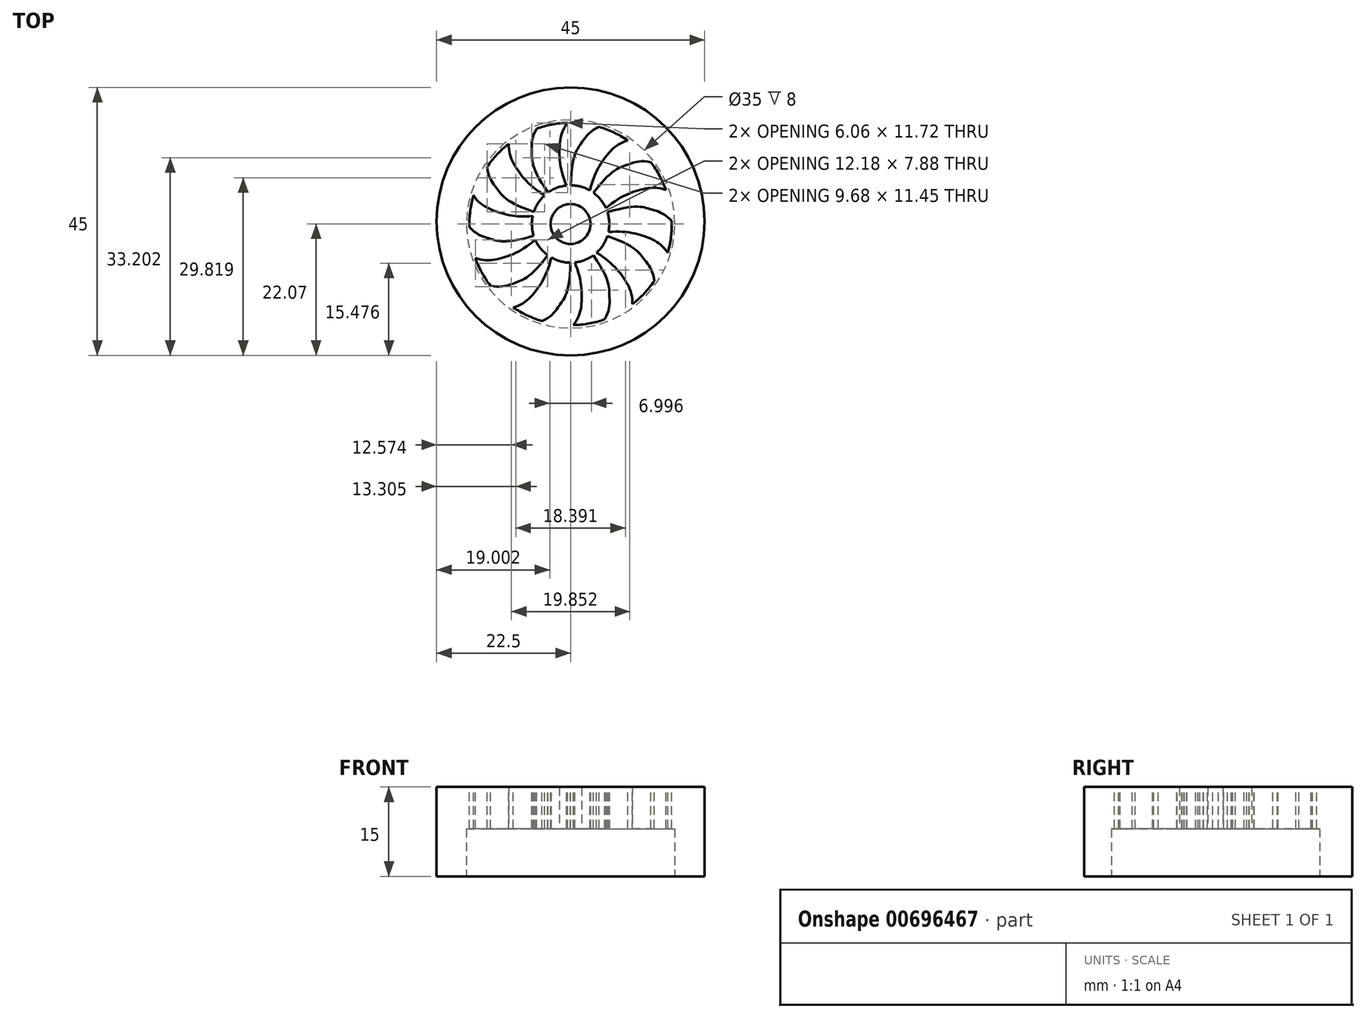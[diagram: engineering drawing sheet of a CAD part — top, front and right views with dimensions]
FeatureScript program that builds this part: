
annotation { "Feature Type Name" : "Feature", "Feature Type Description" : "" }
export const myFeature = defineFeature(function(context is Context, id is Id, definition is map)
    precondition{}
    {
        {
            var Q0;
            Q0=qCreatedBy(makeId("Top.planeOp"),FACE);
            var sketch = newSketch(context, id + "F0", { "sketchPlane" : qUnion([Q0])});
            skCircle(sketch, "E0", {"center": v(0, 0) * mm, "radius": 22.5 * mm});
            skSolve(sketch);
        }
        {
            var Q0;
            Q0=makeQuery(id+"F0.imprint","IMPRINT",FACE,{"disambiguationData":[TD([[makeQuery(id+"F0.imprint","IMPRINT",EDGE,{"derivedFrom":sQuery(id+"F0.wireOp",EDGE,"E0")}),1.0]])]});
            extrude(context, id + "F1", {"entities" : qUnion([Q0]), "depth" : 15 * mm, "offsetDistance" : 25 * mm});
        }
        {
            var Q0;
            Q0=qCreatedBy(makeId("Front.planeOp"),FACE);
            var sketch = newSketch(context, id + "F2", { "sketchPlane" : qUnion([Q0])});
            skLineSegment(sketch, "E1", {"start": v(0, 22.22) * mm, "end": v(0, -15.86) * mm});
            skSolve(sketch);
        }
        {
            var Q0;
            Q0=makeQuery(id+"F1.opExtrude","CAP_FACE",FACE,{"disambiguationData":[OSD([sQuery(id+"F0.wireOp",EDGE,"E0")])],"isStart":false});
            var sketch = newSketch(context, id + "F3", { "sketchPlane" : qUnion([Q0])});
            skFitSpline(sketch, "E2", {"points": [v(0, 5) * mm, v(-1.86, 12.83) * mm, v(0, 17.5) * mm], "startDerivative": vector(-8.9, 17.17) * mm, "endDerivative": vector(9.6, 9.27) * mm});
            skFitSpline(sketch, "E3", {"points": [v(0, 5) * mm, v(1.84, 13.62) * mm, v(5.55, 16.6) * mm], "startDerivative": vector(0, 33.37) * mm, "endDerivative": vector(16.62, 5.33) * mm});
            skArc(sketch, "E4", {"start": v(5.55, 16.6) * mm, "mid": v(2.81, 17.27) * mm, "end": v(0, 17.5) * mm});
            skSolve(sketch);
        }
        {
            var Q0;
            Q0=makeQuery(id+"F3.imprint","IMPRINT",FACE,{"disambiguationData":[TD([[makeQuery(id+"F3.imprint","IMPRINT",EDGE,{"derivedFrom":sQuery(id+"F3.wireOp",EDGE,"E2")}),-1.0]])]});
            var Q1;
            Q1=sQuery(id+"F3.wireOp",EDGE,"E3");
            var Q2;
            Q2=sQuery(id+"F3.wireOp",EDGE,"E2");
            var Q3;
            Q3=sQuery(id+"F3.wireOp",EDGE,"E4");
            extrude(context, id + "F4", {"entities" : qUnion([Q0]), "operationType" : NewBodyOperationType.INTERSECT, "surfaceEntities" : qUnion([Q1, Q2, Q3]), "endBound" : BoundingType.THROUGH_ALL, "oppositeDirection" : true, "depth" : 25 * mm, "offsetDistance" : 25 * mm});
        }
        {
            var Q0;
            Q0=makeQuery(id+"F1.opExtrude","SWEPT_BODY",BODY,{"disambiguationData":[OSD([sQuery(id+"F0.wireOp",EDGE,"E0")])]});
            var Q1;
            Q1=sQuery(id+"F2.wireOp",EDGE,"E1");
            circularPattern(context, id + "F5", {"entities" : qUnion([Q0]), "axis" : qUnion([Q1]), "angle" : 360 * degree, "instanceCount" : 10, "equalSpace" : true});
        }
        {
            var Q0;
            Q0=makeQuery(id+"F3.imprint","IMPRINT",FACE,{"disambiguationData":[TD([[makeQuery(id+"F3.imprint","IMPRINT",EDGE,{"derivedFrom":sQuery(id+"F3.wireOp",EDGE,"E2")}),1.0]])]});
            var sketch = newSketch(context, id + "F6", { "sketchPlane" : qUnion([Q0])});
            skCircle(sketch, "E5", {"center": v(0, 0) * mm, "radius": 17 * mm});
            skCircle(sketch, "E6", {"center": v(0, 0.43) * mm, "radius": 22.5 * mm});
            skSolve(sketch);
        }
        {
            var Q0;
            Q0 = qSketchRegion(id + "F6", true);
            extrude(context, id + "F7", {"entities" : qUnion([Q0]), "operationType" : NewBodyOperationType.ADD, "oppositeDirection" : true, "depth" : 15 * mm, "offsetDistance" : 25 * mm});
        }
        {
            var Q0;
            Q0=makeQuery(id+"F3.imprint","IMPRINT",FACE,{"disambiguationData":[TD([[makeQuery(id+"F3.imprint","IMPRINT",EDGE,{"derivedFrom":sQuery(id+"F3.wireOp",EDGE,"E2")}),-1.0]])]});
            var sketch = newSketch(context, id + "F8", { "sketchPlane" : qUnion([Q0])});
            skCircle(sketch, "E7", {"center": v(0, 0) * mm, "radius": 6.5 * mm});
            skSolve(sketch);
        }
        {
            var Q0;
            Q0 = qSketchRegion(id + "F8", true);
            extrude(context, id + "F9", {"entities" : qUnion([Q0]), "operationType" : NewBodyOperationType.ADD, "oppositeDirection" : true, "depth" : 15 * mm, "offsetDistance" : 25 * mm});
        }
        {
            var Q0;
            {var subQ0=makeQuery(id+"F1.opExtrude","CAP_FACE",FACE,{"disambiguationData":[OSD([sQuery(id+"F0.wireOp",EDGE,"E0")])],"isStart":true});Q0=makeQuery(id+"F9.boolean.opBoolean","MERGE",FACE,{"derivedFrom":[makeQuery(id+"F7.boolean.opBoolean","MERGE",FACE,{"derivedFrom":[subQ0,makeQuery(id+"F5.opPattern","COPY",FACE,{"derivedFrom":subQ0,"instanceName":"1"}),makeQuery(id+"F5.opPattern","COPY",FACE,{"derivedFrom":subQ0,"instanceName":"2"}),makeQuery(id+"F5.opPattern","COPY",FACE,{"derivedFrom":subQ0,"instanceName":"3"}),makeQuery(id+"F5.opPattern","COPY",FACE,{"derivedFrom":subQ0,"instanceName":"4"}),makeQuery(id+"F5.opPattern","COPY",FACE,{"derivedFrom":subQ0,"instanceName":"5"}),makeQuery(id+"F5.opPattern","COPY",FACE,{"derivedFrom":subQ0,"instanceName":"6"}),makeQuery(id+"F5.opPattern","COPY",FACE,{"derivedFrom":subQ0,"instanceName":"7"}),makeQuery(id+"F5.opPattern","COPY",FACE,{"derivedFrom":subQ0,"instanceName":"8"}),makeQuery(id+"F5.opPattern","COPY",FACE,{"derivedFrom":subQ0,"instanceName":"9"}),makeQuery(id+"F7.opExtrude","CAP_FACE",FACE,{"disambiguationData":[OSD([sQuery(id+"F6.wireOp",EDGE,"E5"),sQuery(id+"F6.wireOp",EDGE,"E6")])],"isStart":false})]}),makeQuery(id+"F9.opExtrude","CAP_FACE",FACE,{"disambiguationData":[OSD([sQuery(id+"F8.wireOp",EDGE,"E7")])],"isStart":false})]});}
            var sketch = newSketch(context, id + "F10", { "sketchPlane" : qUnion([Q0])});
            skCircle(sketch, "E8", {"center": v(0, 0) * mm, "radius": 17.5 * mm});
            skSolve(sketch);
        }
        {
            var Q0;
            Q0 = qSketchRegion(id + "F10", true);
            extrude(context, id + "F11", {"entities" : qUnion([Q0]), "operationType" : NewBodyOperationType.REMOVE, "oppositeDirection" : true, "depth" : 8 * mm, "offsetDistance" : 25 * mm});
        }
        {
            var Q0;
            Q0=makeQuery(id+"F3.imprint","IMPRINT",FACE,{"disambiguationData":[TD([[makeQuery(id+"F3.imprint","IMPRINT",EDGE,{"derivedFrom":sQuery(id+"F3.wireOp",EDGE,"E2")}),1.0]])]});
            var sketch = newSketch(context, id + "F12", { "sketchPlane" : qUnion([Q0])});
            skCircle(sketch, "E9", {"center": v(0, 0) * mm, "radius": 3.35 * mm});
            skSolve(sketch);
        }
        {
            var Q0;
            Q0 = qSketchRegion(id + "F12", true);
            extrude(context, id + "F13", {"entities" : qUnion([Q0]), "operationType" : NewBodyOperationType.REMOVE, "endBound" : BoundingType.THROUGH_ALL, "oppositeDirection" : true, "depth" : 25 * mm, "offsetDistance" : 25 * mm});
        }
    });
